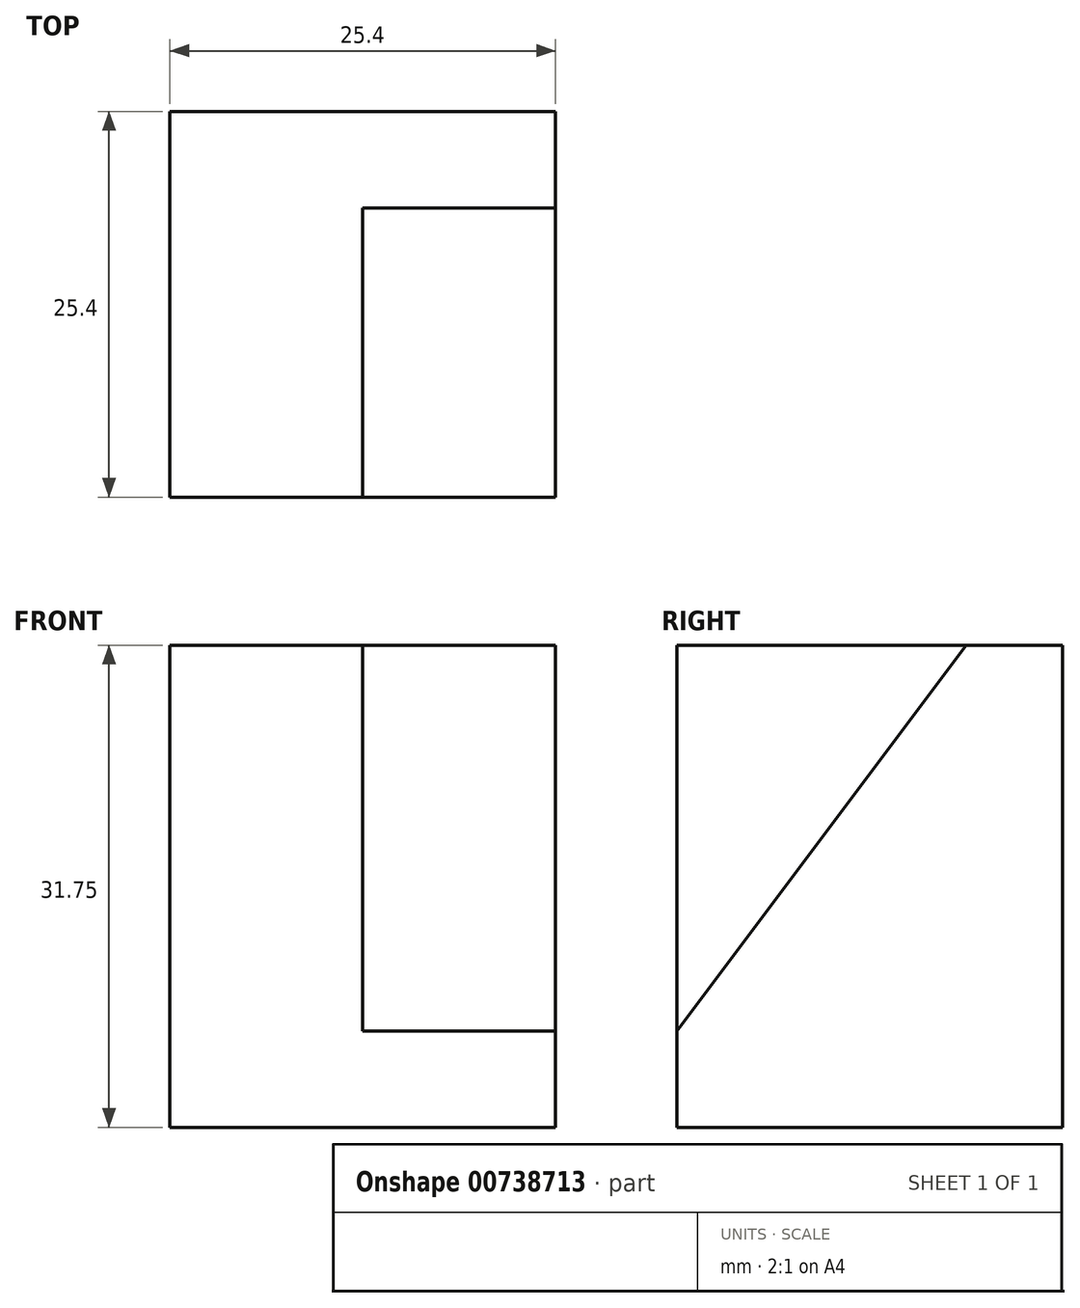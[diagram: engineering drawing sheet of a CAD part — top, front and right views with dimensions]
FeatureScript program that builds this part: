
annotation { "Feature Type Name" : "Feature", "Feature Type Description" : "" }
export const myFeature = defineFeature(function(context is Context, id is Id, definition is map)
    precondition{}
    {
        {
            var Q0;
            Q0=qCreatedBy(makeId("Right.planeOp"),FACE);
            var sketch = newSketch(context, id + "F0", { "sketchPlane" : qUnion([Q0])});
            skLineSegment(sketch, "E0", {"start": v(0, 31.75) * mm, "end": v(25.4, 31.75) * mm});
            skLineSegment(sketch, "E1", {"start": v(25.4, 31.75) * mm, "end": v(25.4, 0) * mm});
            skLineSegment(sketch, "E2", {"start": v(25.4, 0) * mm, "end": v(0, 0) * mm});
            skLineSegment(sketch, "E3", {"start": v(0, 0) * mm, "end": v(0, 31.75) * mm});
            skSolve(sketch);
        }
        {
            var Q0;
            Q0 = qSketchRegion(id + "F0", true);
            extrude(context, id + "F1", {"entities" : qUnion([Q0]), "depth" : 12.7 * mm, "offsetDistance" : 25.4 * mm});
        }
        {
            var Q0;
            Q0=qCreatedBy(makeId("Right.planeOp"),FACE);
            var sketch = newSketch(context, id + "F2", { "sketchPlane" : qUnion([Q0])});
            skLineSegment(sketch, "E4", {"start": v(0, 6.35) * mm, "end": v(19.05, 31.75) * mm});
            skLineSegment(sketch, "E5", {"start": v(19.05, 31.75) * mm, "end": v(25.4, 31.75) * mm});
            skLineSegment(sketch, "E6", {"start": v(25.4, 31.75) * mm, "end": v(25.4, 0) * mm});
            skLineSegment(sketch, "E7", {"start": v(25.4, 0) * mm, "end": v(0, 0) * mm});
            skLineSegment(sketch, "E8", {"start": v(0, 0) * mm, "end": v(0, 6.35) * mm});
            skSolve(sketch);
        }
        {
            var Q0;
            Q0 = qSketchRegion(id + "F2", true);
            extrude(context, id + "F3", {"entities" : qUnion([Q0]), "operationType" : NewBodyOperationType.ADD, "depth" : 25.4 * mm, "offsetDistance" : 25.4 * mm});
        }
    });
